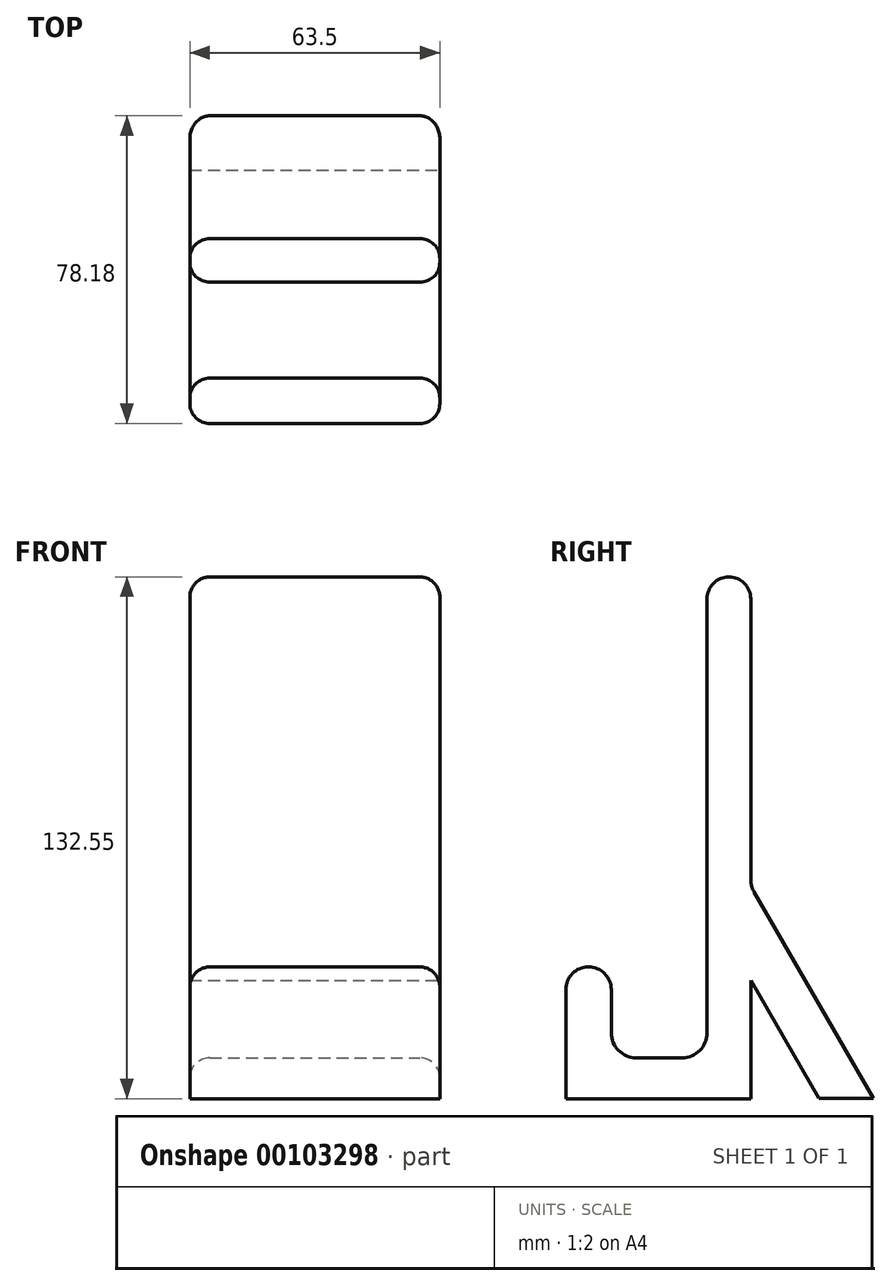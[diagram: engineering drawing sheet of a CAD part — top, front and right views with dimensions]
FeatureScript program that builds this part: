
annotation { "Feature Type Name" : "Feature", "Feature Type Description" : "" }
export const myFeature = defineFeature(function(context is Context, id is Id, definition is map)
    precondition{}
    {
        {
            var Q0;
            Q0=qCreatedBy(makeId("Right.planeOp"),FACE);
            var sketch = newSketch(context, id + "F0", { "sketchPlane" : qUnion([Q0])});
            skLineSegment(sketch, "E0", {"start": v(0, 73.03) * mm, "end": v(0, 1.7) * mm});
            skLineSegment(sketch, "E1", {"start": v(0.85, -1.48) * mm, "end": v(31.19, -53.87) * mm});
            skLineSegment(sketch, "E2", {"start": v(31.19, -53.87) * mm, "end": v(17.32, -53.87) * mm});
            skLineSegment(sketch, "E3", {"start": v(17.32, -53.87) * mm, "end": v(0, -23.96) * mm});
            skLineSegment(sketch, "E4", {"start": v(0, -23.96) * mm, "end": v(0, -53.97) * mm});
            skLineSegment(sketch, "E5", {"start": v(0, -53.97) * mm, "end": v(-46.99, -53.97) * mm});
            skLineSegment(sketch, "E6", {"start": v(-47, -53.97) * mm, "end": v(-47, -26.27) * mm});
            skLineSegment(sketch, "E7", {"start": v(-35.44, -26.27) * mm, "end": v(-35.44, -37.23) * mm});
            skLineSegment(sketch, "E8", {"start": v(-29.1, -43.58) * mm, "end": v(-17.45, -43.58) * mm});
            skLineSegment(sketch, "E9", {"start": v(-11.1, -37.23) * mm, "end": v(-11.1, 73.03) * mm});
            skPoint(sketch, "E10.visualSharp", {"position": v(-11.1, -43.58) * mm});
            skArc(sketch, "E10.filletArc", {"start": v(-17.45, -43.58) * mm, "mid": v(-12.96, -41.72) * mm, "end": v(-11.1, -37.23) * mm});
            skPoint(sketch, "E11.visualSharp", {"position": v(-35.44, -43.58) * mm});
            skArc(sketch, "E11.filletArc", {"start": v(-35.44, -37.23) * mm, "mid": v(-33.58, -41.72) * mm, "end": v(-29.1, -43.58) * mm});
            skArc(sketch, "E12", {"start": v(-35.44, -26.27) * mm, "mid": v(-41.22, -20.5) * mm, "end": v(-47, -26.27) * mm});
            skArc(sketch, "E13", {"start": v(-11.1, 73.03) * mm, "mid": v(-5.55, 78.58) * mm, "end": v(0, 73.03) * mm});
            skPoint(sketch, "E14.visualSharp", {"position": v(0, 0) * mm});
            skArc(sketch, "E14.filletArc", {"start": v(0, 1.7) * mm, "mid": v(0.22, 0.06) * mm, "end": v(0.85, -1.48) * mm});
            skSolve(sketch);
        }
        {
            var Q0;
            Q0=makeQuery(id+"F0.imprint","IMPRINT",FACE,{"disambiguationData":[TD([[makeQuery(id+"F0.imprint","IMPRINT",EDGE,{"derivedFrom":sQuery(id+"F0.wireOp",EDGE,"E0")}),-1.0]])]});
            extrude(context, id + "F1", {"entities" : qUnion([Q0]), "endBound" : BoundingType.SYMMETRIC, "oppositeDirection" : true, "depth" : 63.5 * mm, "hasSecondDirection" : true, "secondDirectionOppositeDirection" : false, "secondDirectionDepth" : 45.5 * mm});
        }
        {
            var Q0;
            Q0=makeQuery(id+"F1.opExtrude","CAP_EDGE",EDGE,{"disambiguationData":[OSD([sQuery(id+"F0.wireOp",EDGE,"E9")])],"isStart":true});
            var Q1;
            Q1=makeQuery(id+"F1.opExtrude","CAP_EDGE",EDGE,{"disambiguationData":[OSD([sQuery(id+"F0.wireOp",EDGE,"E9")])],"isStart":false});
            fillet(context, id + "F2", {"entities" : qUnion([Q0, Q1]), "radius" : 5.08 * mm, "tangentPropagation" : true, "allowEdgeOverflow" : false});
        }
    });
